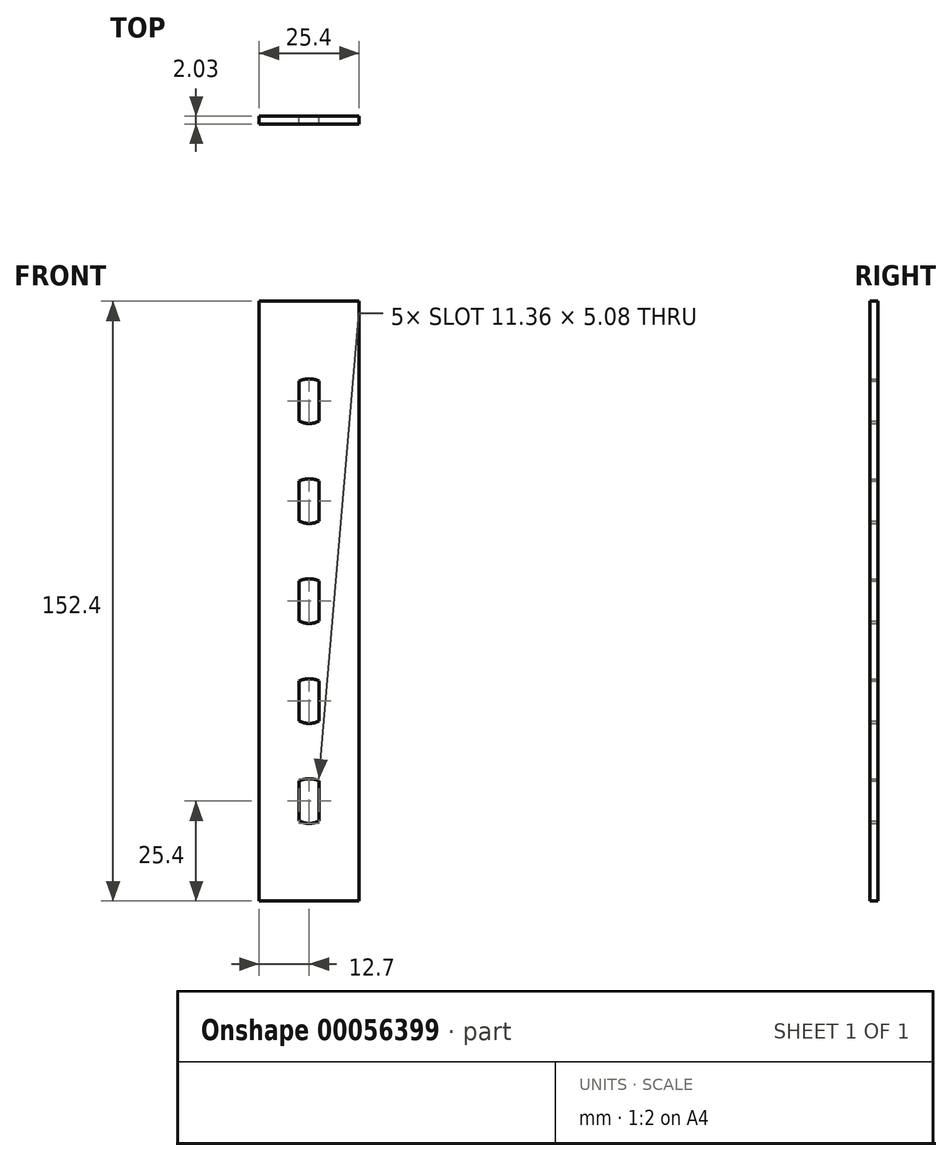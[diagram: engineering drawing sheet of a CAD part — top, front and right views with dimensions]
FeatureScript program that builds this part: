
annotation { "Feature Type Name" : "Feature", "Feature Type Description" : "" }
export const myFeature = defineFeature(function(context is Context, id is Id, definition is map)
    precondition{}
    {
        {
            var Q0;
            Q0=qCreatedBy(makeId("Front.planeOp"),FACE);
            var sketch = newSketch(context, id + "F0", { "sketchPlane" : qUnion([Q0])});
            skLineSegment(sketch, "E0.bottom", {"start": v(0, 0) * mm, "end": v(25.4, 0) * mm});
            skLineSegment(sketch, "E0.top", {"start": v(0, 152.4) * mm, "end": v(25.4, 152.4) * mm});
            skLineSegment(sketch, "E0.left", {"start": v(0, 0) * mm, "end": v(0, 152.4) * mm});
            skLineSegment(sketch, "E0.right", {"start": v(25.4, 0) * mm, "end": v(25.4, 152.4) * mm});
            skLineSegment(sketch, "E1.bottom", {"start": v(12.7, 152.4) * mm, "end": v(12.7, 152.4) * mm});
            skLineSegment(sketch, "E1.top", {"start": v(12.7, 0) * mm, "end": v(12.7, 0) * mm});
            skLineSegment(sketch, "E1.left", {"start": v(12.7, 132.68) * mm, "end": v(12.7, 132.08) * mm, "construction": true});
            skLineSegment(sketch, "E2.bottom", {"start": v(0, 152.4) * mm, "end": v(0, 152.4) * mm});
            skLineSegment(sketch, "E2.top", {"start": v(0, 127) * mm, "end": v(0, 127) * mm});
            skLineSegment(sketch, "E2.left", {"start": v(0, 152.4) * mm, "end": v(0, 127) * mm, "construction": true});
            skLineSegment(sketch, "E2.right", {"start": v(0, 152.4) * mm, "end": v(0, 127) * mm, "construction": true});
            skLineSegment(sketch, "E3.top", {"start": v(0, 101.6) * mm, "end": v(0, 101.6) * mm});
            skLineSegment(sketch, "E3.left", {"start": v(0, 127) * mm, "end": v(0, 101.6) * mm, "construction": true});
            skLineSegment(sketch, "E3.right", {"start": v(0, 127) * mm, "end": v(0, 101.6) * mm, "construction": true});
            skLineSegment(sketch, "E4", {"start": v(0, 101.6) * mm, "end": v(0, 76.2) * mm, "construction": true});
            skLineSegment(sketch, "E5", {"start": v(0, 76.2) * mm, "end": v(0, 50.8) * mm, "construction": true});
            skLineSegment(sketch, "E6", {"start": v(0, 50.8) * mm, "end": v(0, 25.4) * mm, "construction": true});
            skPoint(sketch, "E7", {"position": v(12.7, 127) * mm});
            skPoint(sketch, "E8", {"position": v(12.7, 101.6) * mm});
            skPoint(sketch, "E9", {"position": v(12.7, 76.2) * mm});
            skPoint(sketch, "E10", {"position": v(12.7, 50.8) * mm});
            skPoint(sketch, "E11", {"position": v(12.7, 25.4) * mm});
            skLineSegment(sketch, "E12.rect.bottom", {"start": v(12.9, 132.08) * mm, "end": v(12.7, 132.08) * mm});
            skLineSegment(sketch, "E12.rect.left", {"start": v(15.24, 132.08) * mm, "end": v(15.24, 121.92) * mm});
            skLineSegment(sketch, "E12.rect.right", {"start": v(10.16, 132.08) * mm, "end": v(10.16, 121.92) * mm});
            skLineSegment(sketch, "E13.rect.left", {"start": v(15.24, 106.68) * mm, "end": v(15.24, 96.52) * mm});
            skLineSegment(sketch, "E13.rect.right", {"start": v(10.16, 106.68) * mm, "end": v(10.16, 96.52) * mm});
            skLineSegment(sketch, "E14.rect.left", {"start": v(15.24, 81.28) * mm, "end": v(15.24, 71.12) * mm});
            skLineSegment(sketch, "E14.rect.right", {"start": v(10.16, 81.28) * mm, "end": v(10.16, 71.12) * mm});
            skLineSegment(sketch, "E15.rect.left", {"start": v(15.24, 55.88) * mm, "end": v(15.24, 45.72) * mm});
            skLineSegment(sketch, "E15.rect.right", {"start": v(10.16, 55.88) * mm, "end": v(10.16, 45.72) * mm});
            skLineSegment(sketch, "E16.rect.left", {"start": v(15.24, 30.48) * mm, "end": v(15.24, 20.32) * mm});
            skLineSegment(sketch, "E16.rect.right", {"start": v(10.16, 30.48) * mm, "end": v(10.16, 20.32) * mm});
            skArc(sketch, "E17", {"start": v(15.24, 106.68) * mm, "mid": v(12.7, 107.28) * mm, "end": v(10.16, 106.68) * mm});
            skArc(sketch, "E18", {"start": v(10.16, 71.12) * mm, "mid": v(12.7, 70.52) * mm, "end": v(15.24, 71.12) * mm});
            skArc(sketch, "E19", {"start": v(15.24, 55.88) * mm, "mid": v(12.7, 56.48) * mm, "end": v(10.16, 55.88) * mm});
            skArc(sketch, "E20", {"start": v(15.24, 30.48) * mm, "mid": v(12.7, 31.08) * mm, "end": v(10.16, 30.48) * mm});
            skArc(sketch, "E21", {"start": v(10.16, 121.92) * mm, "mid": v(12.7, 121.32) * mm, "end": v(15.24, 121.92) * mm});
            skLineSegment(sketch, "E22.trimOffspring", {"start": v(12.7, 121.92) * mm, "end": v(12.7, 121.32) * mm, "construction": true});
            skLineSegment(sketch, "E23.trimOffspring", {"start": v(12.7, 132.08) * mm, "end": v(12.7, 132.08) * mm, "construction": true});
            skArc(sketch, "E24.trimOffspring", {"start": v(15.24, 132.08) * mm, "mid": v(12.7, 132.68) * mm, "end": v(10.16, 132.08) * mm});
            skArc(sketch, "E25.trimOffspring", {"start": v(10.16, 96.52) * mm, "mid": v(12.7, 95.92) * mm, "end": v(15.24, 96.52) * mm});
            skArc(sketch, "E26.trimOffspring", {"start": v(15.24, 81.28) * mm, "mid": v(12.7, 81.88) * mm, "end": v(10.16, 81.28) * mm});
            skArc(sketch, "E27.trimOffspring", {"start": v(10.16, 45.72) * mm, "mid": v(12.7, 45.12) * mm, "end": v(15.24, 45.72) * mm});
            skArc(sketch, "E28.trimOffspring", {"start": v(10.16, 20.32) * mm, "mid": v(12.7, 19.72) * mm, "end": v(15.24, 20.32) * mm});
            skSolve(sketch);
        }
        {
            var Q0;
            Q0 = qSketchRegion(id + "F0", true);
            extrude(context, id + "F1", {"entities" : qUnion([Q0]), "depth" : 2.03 * mm});
        }
    });
